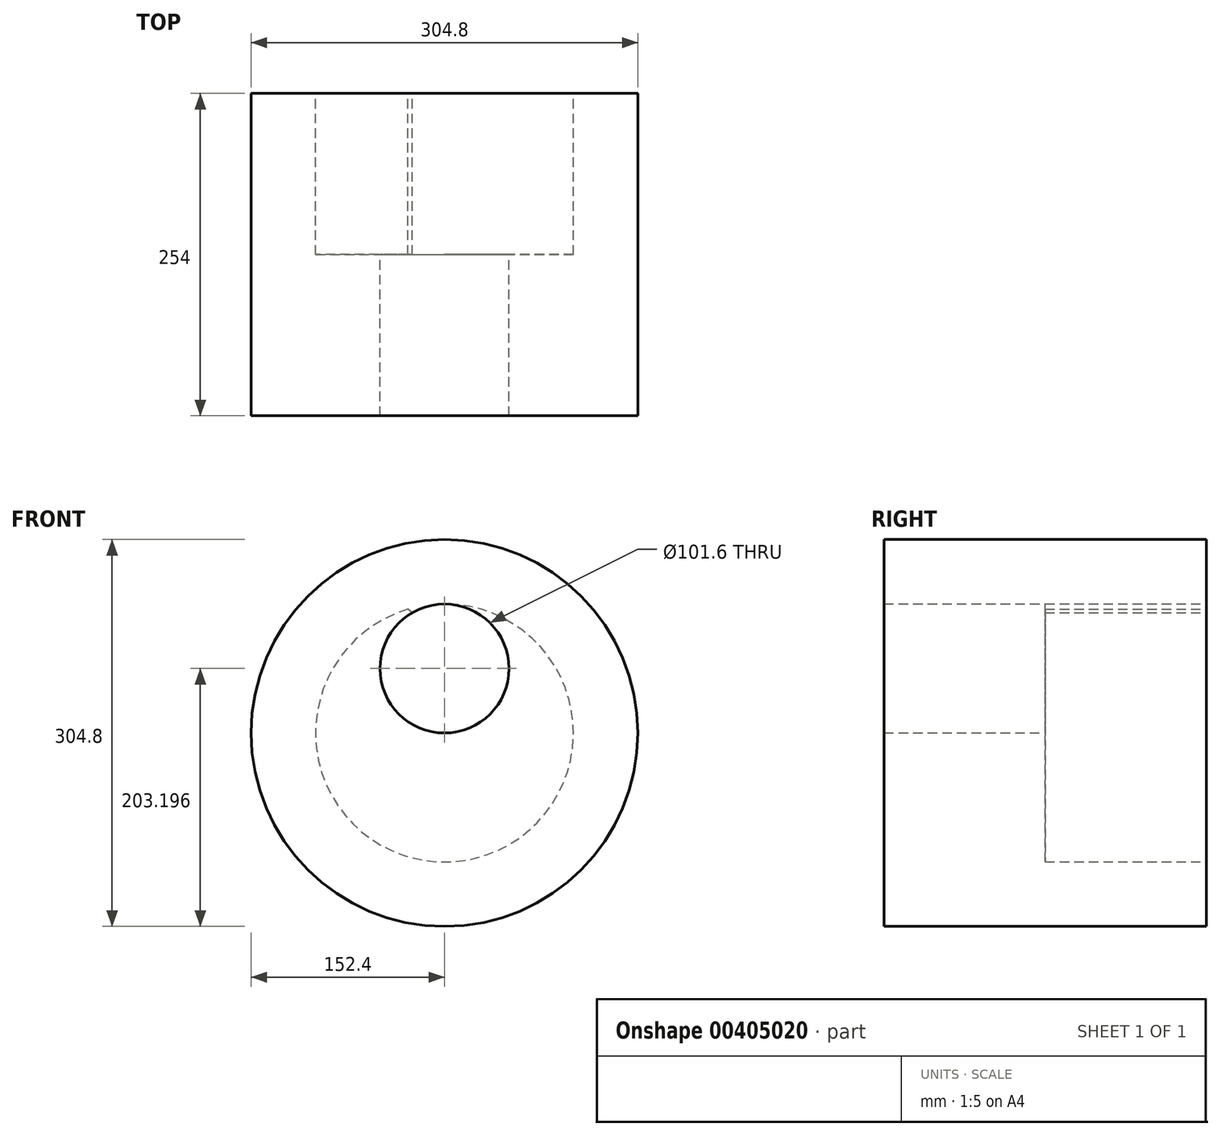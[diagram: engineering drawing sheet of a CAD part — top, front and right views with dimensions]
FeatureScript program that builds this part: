
annotation { "Feature Type Name" : "Feature", "Feature Type Description" : "" }
export const myFeature = defineFeature(function(context is Context, id is Id, definition is map)
    precondition{}
    {
        {
            var Q0;
            Q0=qCreatedBy(makeId("Front.planeOp"),FACE);
            var sketch = newSketch(context, id + "F0", { "sketchPlane" : qUnion([Q0])});
            skCircle(sketch, "E0", {"center": v(0, 0) * mm, "radius": 0.8 * mm});
            skCircle(sketch, "E1", {"center": v(0, -0.8) * mm, "radius": 1.59 * mm});
            skCircle(sketch, "E2", {"center": v(0, -0.8) * mm, "radius": 50.8 * mm});
            skCircle(sketch, "E3", {"center": v(0, -51.6) * mm, "radius": 101.6 * mm});
            skCircle(sketch, "E4", {"center": v(0, -51.6) * mm, "radius": 152.4 * mm});
            skLineSegment(sketch, "E5", {"start": v(-25.52, 43.13) * mm, "end": v(-28.74, 45.86) * mm});
            skSolve(sketch);
        }
        {
            var Q0;
            Q0=makeQuery(id+"F0.imprint","IMPRINT",FACE,{"disambiguationData":[TD([[makeQuery(id+"F0.imprint","IMPRINT",EDGE,{"derivedFrom":sQuery(id+"F0.wireOp",EDGE,"E3")}),-1.0]])]});
            var Q1;
            Q1=makeQuery(id+"F0.imprint","IMPRINT",FACE,{"disambiguationData":[TD([[makeQuery(id+"F0.imprint","IMPRINT",EDGE,{"derivedFrom":sQuery(id+"F0.wireOp",EDGE,"E2")}),-1.0]])]});
            extrude(context, id + "F1", {"entities" : qUnion([Q0, Q1]), "depth" : 254 * mm});
        }
        {
            var Q0;
            {var subQ0=sQuery(id+"F0.wireOp",EDGE,"E5");Q0=makeQuery(id+"F0.imprint","IMPRINT",FACE,{"disambiguationData":[TD([[makeQuery(id+"F0.imprint","IMPRINT",EDGE,{"derivedFrom":subQ0}),1.0]])]});}
            extrude(context, id + "F2", {"entities" : qUnion([Q0]), "operationType" : NewBodyOperationType.REMOVE, "depth" : 127 * mm});
        }
    });
